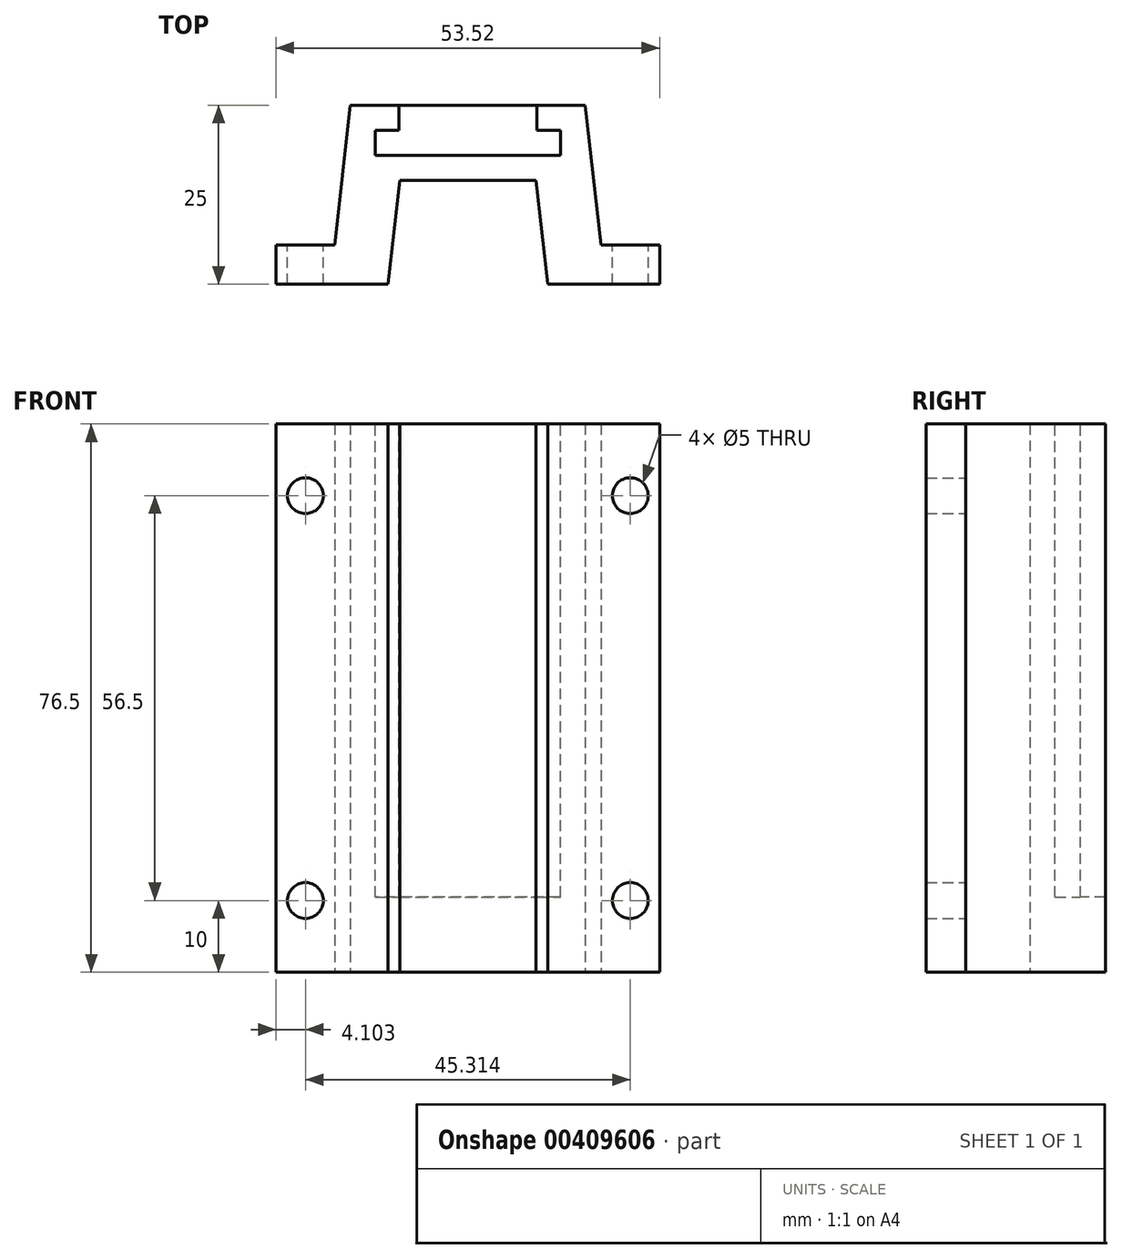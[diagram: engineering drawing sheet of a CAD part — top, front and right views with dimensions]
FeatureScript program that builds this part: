
annotation { "Feature Type Name" : "Feature", "Feature Type Description" : "" }
export const myFeature = defineFeature(function(context is Context, id is Id, definition is map)
    precondition{}
    {
        {
            var Q0;
            Q0=qCreatedBy(makeId("Top.planeOp"),FACE);
            var sketch = newSketch(context, id + "F0", { "sketchPlane" : qUnion([Q0])});
            skLineSegment(sketch, "E0", {"start": v(16.38, 0) * mm, "end": v(18.56, -19.5) * mm});
            skLineSegment(sketch, "E1", {"start": v(18.56, -19.5) * mm, "end": v(26.76, -19.5) * mm});
            skLineSegment(sketch, "E2", {"start": v(26.76, -19.5) * mm, "end": v(26.76, -25) * mm});
            skLineSegment(sketch, "E3", {"start": v(26.76, -25) * mm, "end": v(11.12, -25) * mm});
            skLineSegment(sketch, "E4", {"start": v(9.5, -10.5) * mm, "end": v(11.12, -25) * mm});
            skLineSegment(sketch, "E5", {"start": v(0, 0) * mm, "end": v(16.38, 0) * mm});
            skLineSegment(sketch, "E6", {"start": v(9.5, -10.5) * mm, "end": v(0, -10.5) * mm});
            skLineSegment(sketch, "E7.MirrorCS", {"start": v(-18.56, -19.5) * mm, "end": v(-26.76, -19.5) * mm});
            skLineSegment(sketch, "E8.MirrorCS", {"start": v(-26.76, -25) * mm, "end": v(-11.12, -25) * mm});
            skLineSegment(sketch, "E9.MirrorCS", {"start": v(-9.5, -10.5) * mm, "end": v(0, -10.5) * mm});
            skLineSegment(sketch, "E10.MirrorCS", {"start": v(-26.76, -19.5) * mm, "end": v(-26.76, -25) * mm});
            skLineSegment(sketch, "E11.MirrorCS", {"start": v(-16.38, 0) * mm, "end": v(-18.56, -19.5) * mm});
            skLineSegment(sketch, "E12.MirrorCS", {"start": v(-9.5, -10.5) * mm, "end": v(-11.12, -25) * mm});
            skLineSegment(sketch, "E13.MirrorCS", {"start": v(0, 0) * mm, "end": v(-16.38, 0) * mm});
            skSolve(sketch);
        }
        {
            var Q0;
            Q0=qSketchRegion(id+"F0",true);
            extrude(context, id + "F1", {"entities" : qUnion([Q0]), "depth" : 76.5 * mm});
        }
        {
            var Q0;
            Q0=makeQuery(id+"F1.opExtrude","CAP_FACE",FACE,{"disambiguationData":[OSD([sQuery(id+"F0.wireOp",EDGE,"E0"),sQuery(id+"F0.wireOp",EDGE,"E1"),sQuery(id+"F0.wireOp",EDGE,"E2"),sQuery(id+"F0.wireOp",EDGE,"E3"),sQuery(id+"F0.wireOp",EDGE,"E4"),sQuery(id+"F0.wireOp",EDGE,"E5"),sQuery(id+"F0.wireOp",EDGE,"E6"),sQuery(id+"F0.wireOp",EDGE,"E7.MirrorCS"),sQuery(id+"F0.wireOp",EDGE,"E8.MirrorCS"),sQuery(id+"F0.wireOp",EDGE,"E9.MirrorCS"),sQuery(id+"F0.wireOp",EDGE,"E10.MirrorCS"),sQuery(id+"F0.wireOp",EDGE,"E11.MirrorCS"),sQuery(id+"F0.wireOp",EDGE,"E12.MirrorCS"),sQuery(id+"F0.wireOp",EDGE,"E13.MirrorCS")])],"isStart":false});
            var sketch = newSketch(context, id + "F2", { "sketchPlane" : qUnion([Q0])});
            skLineSegment(sketch, "E14", {"start": v(-9.6, 0) * mm, "end": v(9.6, 0) * mm});
            skLineSegment(sketch, "E15", {"start": v(9.6, 0) * mm, "end": v(9.6, -3.5) * mm});
            skLineSegment(sketch, "E16", {"start": v(9.6, -3.5) * mm, "end": v(12.9, -3.5) * mm});
            skLineSegment(sketch, "E17", {"start": v(12.9, -3.5) * mm, "end": v(12.9, -7) * mm});
            skLineSegment(sketch, "E18", {"start": v(12.9, -7) * mm, "end": v(-12.9, -7) * mm});
            skLineSegment(sketch, "E19", {"start": v(-12.9, -7) * mm, "end": v(-12.9, -3.5) * mm});
            skLineSegment(sketch, "E20", {"start": v(-12.9, -3.5) * mm, "end": v(-9.6, -3.5) * mm});
            skLineSegment(sketch, "E21", {"start": v(-9.6, -3.5) * mm, "end": v(-9.6, 0) * mm});
            skLineSegment(sketch, "E22", {"start": v(0, 0) * mm, "end": v(0, -10.5) * mm, "construction": true});
            skLineSegment(sketch, "E23", {"start": v(0, -7) * mm, "end": v(0, -4.27) * mm, "construction": true});
            skSolve(sketch);
        }
        {
            var Q0;
            Q0=qSketchRegion(id+"F2",true);
            extrude(context, id + "F3", {"entities" : qUnion([Q0]), "operationType" : NewBodyOperationType.REMOVE, "oppositeDirection" : true, "depth" : 66 * mm});
        }
        {
            var Q0;
            Q0=makeQuery(id+"F1.opExtrude","SWEPT_FACE",FACE,{"disambiguationData":[OSD([sQuery(id+"F0.wireOp",EDGE,"E7.MirrorCS")])]});
            var sketch = newSketch(context, id + "F4", { "sketchPlane" : qUnion([Q0])});
            skCircle(sketch, "E24", {"center": v(22.66, 10) * mm, "radius": 2.5 * mm});
            skPoint(sketch, "E25.0", {"position": v(22.66, 0) * mm});
            skLineSegment(sketch, "E26", {"start": v(22.66, 0) * mm, "end": v(22.66, 76.5) * mm, "construction": true});
            skLineSegment(sketch, "E27", {"start": v(18.56, 38.25) * mm, "end": v(26.76, 38.25) * mm, "construction": true});
            skLineSegment(sketch, "E28.MirrorCS", {"start": v(22.66, 76.5) * mm, "end": v(22.66, 0) * mm, "construction": true});
            skCircle(sketch, "E29.MirrorC", {"center": v(22.66, 66.5) * mm, "radius": 2.5 * mm});
            skLineSegment(sketch, "E30.MirrorCS", {"start": v(-18.56, 38.25) * mm, "end": v(-26.76, 38.25) * mm, "construction": true});
            skCircle(sketch, "E31.MirrorC", {"center": v(-22.66, 10) * mm, "radius": 2.5 * mm});
            skCircle(sketch, "E32.MirrorC", {"center": v(-22.66, 66.5) * mm, "radius": 2.5 * mm});
            skSolve(sketch);
        }
        {
            var Q0;
            Q0 = qSketchRegion(id + "F4", true);
            extrude(context, id + "F5", {"entities" : qUnion([Q0]), "operationType" : NewBodyOperationType.REMOVE, "endBound" : BoundingType.THROUGH_ALL, "oppositeDirection" : true, "depth" : 25 * mm});
        }
    });
